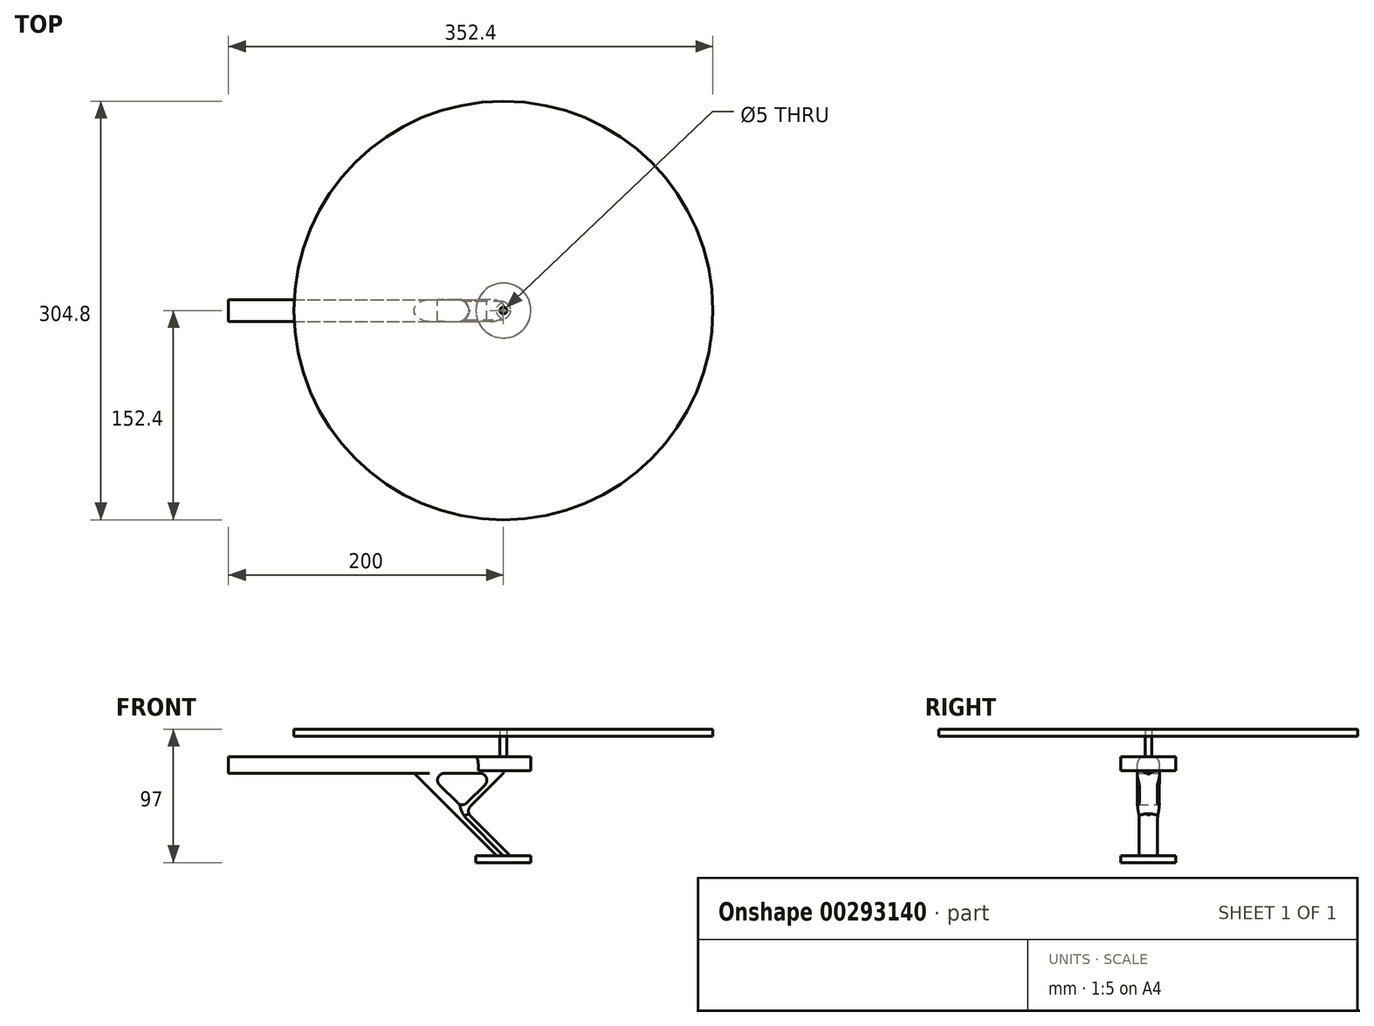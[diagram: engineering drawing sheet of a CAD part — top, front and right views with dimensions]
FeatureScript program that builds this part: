
annotation { "Feature Type Name" : "Feature", "Feature Type Description" : "" }
export const myFeature = defineFeature(function(context is Context, id is Id, definition is map)
    precondition{}
    {
        {
            var Q0;
            Q0=qCreatedBy(makeId("Front.planeOp"),FACE);
            var sketch = newSketch(context, id + "F0", { "sketchPlane" : qUnion([Q0])});
            skLineSegment(sketch, "E0.bottom", {"start": v(0, 0) * mm, "end": v(200, 0) * mm});
            skLineSegment(sketch, "E0.top", {"start": v(0, 12) * mm, "end": v(200, 12) * mm});
            skLineSegment(sketch, "E0.left", {"start": v(0, 0) * mm, "end": v(0, 12) * mm});
            skLineSegment(sketch, "E0.right", {"start": v(200, 0) * mm, "end": v(200, 12) * mm});
            skSolve(sketch);
        }
        {
            var Q0;
            Q0=makeQuery(id+"F0.imprint","IMPRINT",FACE,{"disambiguationData":[TD([[makeQuery(id+"F0.imprint","IMPRINT",EDGE,{"derivedFrom":sQuery(id+"F0.wireOp",EDGE,"E0.bottom")}),1.0]])]});
            extrude(context, id + "F1", {"entities" : qUnion([Q0]), "oppositeDirection" : true, "depth" : 16 * mm});
        }
        {
            var Q0;
            Q0=makeQuery(id+"F1.opExtrude","SWEPT_FACE",FACE,{"disambiguationData":[OSD([sQuery(id+"F0.wireOp",EDGE,"E0.top")])]});
            var sketch = newSketch(context, id + "F2", { "sketchPlane" : qUnion([Q0])});
            skCircle(sketch, "E1", {"center": v(200, 8) * mm, "radius": 20 * mm});
            skSolve(sketch);
        }
        {
            var Q0;
            {var subQ1=sQuery(id+"F0.wireOp",EDGE,"E0.top");var subQ6=makeQuery(id+"F1.opExtrude","SWEPT_EDGE",EDGE,{"disambiguationData":[OSD([subQ1,sQuery(id+"F0.wireOp",EDGE,"E0.right")])]});Q0=makeQuery(id+"F2.imprint","IMPRINT",FACE,{"disambiguationData":[TD([[makeQuery(id+"F2.imprint","IMPRINT",EDGE,{"derivedFrom":subQ6}),1.0]])]});}
            var Q1;
            {var subQ1=sQuery(id+"F0.wireOp",EDGE,"E0.top");var subQ6=makeQuery(id+"F1.opExtrude","SWEPT_EDGE",EDGE,{"disambiguationData":[OSD([subQ1,sQuery(id+"F0.wireOp",EDGE,"E0.right")])]});Q1=makeQuery(id+"F2.imprint","IMPRINT",FACE,{"disambiguationData":[TD([[makeQuery(id+"F2.imprint","IMPRINT",EDGE,{"derivedFrom":subQ6}),-1.0]])]});}
            extrude(context, id + "F3", {"entities" : qUnion([Q0, Q1]), "operationType" : NewBodyOperationType.ADD, "oppositeDirection" : true, "depth" : 10 * mm});
        }
        {
            var Q0;
            Q0=makeQuery(id+"F1.opExtrude","CAP_FACE",FACE,{"disambiguationData":[OSD([sQuery(id+"F0.wireOp",EDGE,"E0.bottom"),sQuery(id+"F0.wireOp",EDGE,"E0.top"),sQuery(id+"F0.wireOp",EDGE,"E0.left"),sQuery(id+"F0.wireOp",EDGE,"E0.right")])],"isStart":true});
            var sketch = newSketch(context, id + "F4", { "sketchPlane" : qUnion([Q0])});
            skLineSegment(sketch, "E2", {"start": v(135, 0) * mm, "end": v(195, -60) * mm});
            skLineSegment(sketch, "E3", {"start": v(205, -60) * mm, "end": v(145, 0) * mm});
            skLineSegment(sketch, "E4", {"start": v(195, -60) * mm, "end": v(205, -60) * mm});
            skLineSegment(sketch, "E5", {"start": v(135, 0) * mm, "end": v(145, 0) * mm});
            skLineSegment(sketch, "E6", {"start": v(200, 0) * mm, "end": v(172.5, -27.5) * mm});
            skLineSegment(sketch, "E7", {"start": v(200, 0) * mm, "end": v(195, 0) * mm});
            skLineSegment(sketch, "E8", {"start": v(195, 0) * mm, "end": v(170, -25) * mm});
            skSolve(sketch);
        }
        {
            var Q0;
            Q0=makeQuery(id+"F4.imprint","IMPRINT",FACE,{"disambiguationData":[TD([[makeQuery(id+"F4.imprint","IMPRINT",EDGE,{"derivedFrom":sQuery(id+"F4.wireOp",EDGE,"E2")}),1.0]])]});
            var Q1;
            {var subQ0=sQuery(id+"F4.wireOp",EDGE,"E6");Q1=makeQuery(id+"F4.imprint","IMPRINT",FACE,{"disambiguationData":[TD([[makeQuery(id+"F4.imprint","IMPRINT",EDGE,{"derivedFrom":subQ0}),-1.0]])]});}
            extrude(context, id + "F5", {"entities" : qUnion([Q0, Q1]), "operationType" : NewBodyOperationType.ADD, "oppositeDirection" : true, "depth" : 16 * mm});
        }
        {
            var Q0;
            Q0=makeQuery(id+"F5.opExtrude","SWEPT_EDGE",EDGE,{"disambiguationData":[OSD([sQuery(id+"F4.wireOp",EDGE,"E3"),sQuery(id+"F4.wireOp",EDGE,"E8")])]});
            var Q1;
            Q1=makeQuery(id+"F5.opExtrude","SWEPT_EDGE",EDGE,{"disambiguationData":[OSD([sQuery(id+"F0.wireOp",EDGE,"E0.bottom"),sQuery(id+"F4.wireOp",EDGE,"E3"),sQuery(id+"F4.wireOp",EDGE,"E5")])]});
            var Q2;
            Q2=makeQuery(id+"F5.opExtrude","SWEPT_EDGE",EDGE,{"disambiguationData":[OSD([sQuery(id+"F0.wireOp",EDGE,"E0.bottom"),sQuery(id+"F4.wireOp",EDGE,"E7"),sQuery(id+"F4.wireOp",EDGE,"E8")])]});
            var Q3;
            Q3=makeQuery(id+"F5.opExtrude","SWEPT_EDGE",EDGE,{"disambiguationData":[OSD([sQuery(id+"F4.wireOp",EDGE,"E3"),sQuery(id+"F4.wireOp",EDGE,"E6")])]});
            var Q4;
            Q4=makeQuery(id+"F5.opExtrude","SWEPT_EDGE",EDGE,{"disambiguationData":[OSD([sQuery(id+"F0.wireOp",EDGE,"E0.bottom"),sQuery(id+"F4.wireOp",EDGE,"E2"),sQuery(id+"F4.wireOp",EDGE,"E5")])]});
            fillet(context, id + "F6", {"entities" : qUnion([Q0, Q1, Q2, Q3, Q4]), "radius" : 5 * mm, "tangentPropagation" : true, "allowEdgeOverflow" : false});
        }
        {
            var Q0;
            Q0=makeQuery(id+"F5.opExtrude","SWEPT_FACE",FACE,{"disambiguationData":[OSD([sQuery(id+"F4.wireOp",EDGE,"E4")])]});
            var sketch = newSketch(context, id + "F7", { "sketchPlane" : qUnion([Q0])});
            skCircle(sketch, "E9", {"center": v(200, -8) * mm, "radius": 20 * mm});
            skSolve(sketch);
        }
        {
            var Q0;
            Q0=makeQuery(id+"F7.imprint","IMPRINT",FACE,{"disambiguationData":[TD([[makeQuery(id+"F7.imprint","IMPRINT",EDGE,{"derivedFrom":sQuery(id+"F7.wireOp",EDGE,"E9")}),1.0]])]});
            var Q1;
            {var subQ0=sQuery(id+"F4.wireOp",EDGE,"E4");Q1=makeQuery(id+"F7.imprint","IMPRINT",FACE,{"disambiguationData":[TD([[makeQuery(id+"F7.imprint","IMPRINT",EDGE,{"derivedFrom":makeQuery(id+"F5.opExtrude","CAP_EDGE",EDGE,{"disambiguationData":[OSD([subQ0])],"isStart":true})}),-1.0]])]});}
            extrude(context, id + "F8", {"entities" : qUnion([Q0, Q1]), "operationType" : NewBodyOperationType.ADD, "depth" : 5 * mm});
        }
        {
            var Q0;
            {var subQ0=sQuery(id+"F0.wireOp",EDGE,"E0.right");Q0=makeQuery(id+"F5.boolean.opBoolean","MERGE",EDGE,{"derivedFrom":[makeQuery(id+"F1.opExtrude","SWEPT_EDGE",EDGE,{"disambiguationData":[OSD([sQuery(id+"F0.wireOp",EDGE,"E0.bottom"),subQ0])]}),makeQuery(id+"F5.opExtrude","SWEPT_EDGE",EDGE,{"disambiguationData":[OSD([subQ0,sQuery(id+"F4.wireOp",EDGE,"E6"),sQuery(id+"F4.wireOp",EDGE,"E7")])]})]});}
            fillet(context, id + "F9", {"entities" : qUnion([Q0]), "radius" : 2 * mm, "tangentPropagation" : true, "allowEdgeOverflow" : false});
        }
        {
            var Q0;
            Q0=makeQuery(id+"F3.boolean.opBoolean","MERGE",FACE,{"derivedFrom":[makeQuery(id+"F1.opExtrude","SWEPT_FACE",FACE,{"disambiguationData":[OSD([sQuery(id+"F0.wireOp",EDGE,"E0.top")])]}),makeQuery(id+"F3.opExtrude","CAP_FACE",FACE,{"disambiguationData":[OSD([sQuery(id+"F2.wireOp",EDGE,"E1")])],"isStart":true})]});
            var sketch = newSketch(context, id + "F10", { "sketchPlane" : qUnion([Q0])});
            skCircle(sketch, "E10", {"center": v(200, 8) * mm, "radius": 2.5 * mm});
            skSolve(sketch);
        }
        {
            var Q0;
            Q0=makeQuery(id+"F10.imprint","IMPRINT",FACE,{"disambiguationData":[TD([[makeQuery(id+"F10.imprint","IMPRINT",EDGE,{"derivedFrom":sQuery(id+"F10.wireOp",EDGE,"E10")}),1.0]])]});
            extrude(context, id + "F11", {"entities" : qUnion([Q0]), "operationType" : NewBodyOperationType.ADD, "depth" : 15 * mm});
        }
        {
            var Q0;
            Q0=makeQuery(id+"F11.opExtrude","CAP_FACE",FACE,{"disambiguationData":[OSD([sQuery(id+"F10.wireOp",EDGE,"E10")])],"isStart":false});
            var sketch = newSketch(context, id + "F12", { "sketchPlane" : qUnion([Q0])});
            skCircle(sketch, "E11", {"center": v(200, 8) * mm, "radius": 152.4 * mm});
            skSolve(sketch);
        }
        {
            var Q0;
            Q0=makeQuery(id+"F1.opExtrude","CAP_EDGE",EDGE,{"disambiguationData":[OSD([sQuery(id+"F0.wireOp",EDGE,"E0.top")])],"isStart":false});
            var Q1;
            Q1=makeQuery(id+"F1.opExtrude","CAP_EDGE",EDGE,{"disambiguationData":[OSD([sQuery(id+"F0.wireOp",EDGE,"E0.top")])],"isStart":true});
            fillet(context, id + "F13", {"entities" : qUnion([Q0, Q1]), "radius" : 5 * mm, "tangentPropagation" : true, "allowEdgeOverflow" : false});
        }
        {
            var Q0;
            Q0=makeQuery(id+"F5.opExtrude","CAP_EDGE",EDGE,{"disambiguationData":[OSD([sQuery(id+"F4.wireOp",EDGE,"E6")])],"isStart":false});
            var Q1;
            Q1=makeQuery(id+"F5.opExtrude","CAP_EDGE",EDGE,{"disambiguationData":[OSD([sQuery(id+"F4.wireOp",EDGE,"E6")])],"isStart":true});
            fillet(context, id + "F14", {"entities" : qUnion([Q0, Q1]), "radius" : 8 * mm, "tangentPropagation" : true, "allowEdgeOverflow" : false});
        }
        {
            var Q0;
            Q0=makeQuery(id+"F5.opExtrude","CAP_EDGE",EDGE,{"disambiguationData":[OSD([sQuery(id+"F4.wireOp",EDGE,"E2")])],"isStart":false});
            var Q1;
            {var subQ0=sQuery(id+"F4.wireOp",EDGE,"E2");var subQ1=sQuery(id+"F4.wireOp",EDGE,"E6");var subQ2=sQuery(id+"F4.wireOp",EDGE,"E3");Q1=makeQuery(id+"F14.opFillet","BLEND_EDGE",EDGE,{"blendedFrom":[makeQuery(id+"F6.opFillet","BLEND_EDGE",EDGE,{"blendedFrom":[makeQuery(id+"F5.opExtrude","SWEPT_EDGE",EDGE,{"disambiguationData":[OSD([subQ2,subQ1])]}),makeQuery(id+"F5.boolean.opBoolean","MERGE",FACE,{"derivedFrom":[makeQuery(id+"F1.opExtrude","CAP_FACE",FACE,{"disambiguationData":[OSD([sQuery(id+"F0.wireOp",EDGE,"E0.bottom"),sQuery(id+"F0.wireOp",EDGE,"E0.top"),sQuery(id+"F0.wireOp",EDGE,"E0.left"),sQuery(id+"F0.wireOp",EDGE,"E0.right")])],"isStart":false}),makeQuery(id+"F5.opExtrude","CAP_FACE",FACE,{"disambiguationData":[OSD([subQ0,subQ2,sQuery(id+"F4.wireOp",EDGE,"E4"),sQuery(id+"F4.wireOp",EDGE,"E5"),subQ1,sQuery(id+"F4.wireOp",EDGE,"E7"),sQuery(id+"F4.wireOp",EDGE,"E8")])],"isStart":false})]})],"blendedInto":[makeQuery(id+"F5.boolean.opBoolean","MERGE",FACE,{"derivedFrom":[makeQuery(id+"F1.opExtrude","CAP_FACE",FACE,{"disambiguationData":[OSD([sQuery(id+"F0.wireOp",EDGE,"E0.bottom"),sQuery(id+"F0.wireOp",EDGE,"E0.top"),sQuery(id+"F0.wireOp",EDGE,"E0.left"),sQuery(id+"F0.wireOp",EDGE,"E0.right")])],"isStart":false}),makeQuery(id+"F5.opExtrude","CAP_FACE",FACE,{"disambiguationData":[OSD([subQ0,subQ2,sQuery(id+"F4.wireOp",EDGE,"E4"),sQuery(id+"F4.wireOp",EDGE,"E5"),subQ1,sQuery(id+"F4.wireOp",EDGE,"E7"),sQuery(id+"F4.wireOp",EDGE,"E8")])],"isStart":false})]})]}),makeQuery(id+"F5.opExtrude","SWEPT_FACE",FACE,{"disambiguationData":[OSD([subQ0])]})],"blendedInto":[makeQuery(id+"F5.opExtrude","SWEPT_FACE",FACE,{"disambiguationData":[OSD([subQ0])]})]});}
            var Q2;
            {var subQ0=sQuery(id+"F4.wireOp",EDGE,"E3");Q2=makeQuery(id+"F14.opFillet","BLEND_EDGE",EDGE,{"blendedFrom":[makeQuery(id+"F5.opExtrude","CAP_EDGE",EDGE,{"disambiguationData":[OSD([subQ0]),TDD([makeQuery(id+"F4.imprint","IMPRINT",EDGE,{"disambiguationData":[TD([[makeQuery(id+"F4.imprint","INTERSECT",VERTEX,{"derivedFrom":[subQ0,sQuery(id+"F4.wireOp",EDGE,"E4")]}),-1.0]])],"derivedFrom":subQ0})])],"isStart":false}),makeQuery(id+"F5.opExtrude","SWEPT_FACE",FACE,{"disambiguationData":[OSD([sQuery(id+"F4.wireOp",EDGE,"E2")])]})],"blendedInto":[makeQuery(id+"F5.opExtrude","SWEPT_FACE",FACE,{"disambiguationData":[OSD([sQuery(id+"F4.wireOp",EDGE,"E2")])]})]});}
            var Q3;
            Q3=makeQuery(id+"F5.opExtrude","CAP_EDGE",EDGE,{"disambiguationData":[OSD([sQuery(id+"F4.wireOp",EDGE,"E2")])],"isStart":true});
            var Q4;
            {var subQ0=sQuery(id+"F4.wireOp",EDGE,"E2");var subQ1=sQuery(id+"F4.wireOp",EDGE,"E6");var subQ2=sQuery(id+"F4.wireOp",EDGE,"E3");Q4=makeQuery(id+"F14.opFillet","BLEND_EDGE",EDGE,{"blendedFrom":[makeQuery(id+"F6.opFillet","BLEND_EDGE",EDGE,{"blendedFrom":[makeQuery(id+"F5.opExtrude","SWEPT_EDGE",EDGE,{"disambiguationData":[OSD([subQ2,subQ1])]}),makeQuery(id+"F5.boolean.opBoolean","MERGE",FACE,{"derivedFrom":[makeQuery(id+"F1.opExtrude","CAP_FACE",FACE,{"disambiguationData":[OSD([sQuery(id+"F0.wireOp",EDGE,"E0.bottom"),sQuery(id+"F0.wireOp",EDGE,"E0.top"),sQuery(id+"F0.wireOp",EDGE,"E0.left"),sQuery(id+"F0.wireOp",EDGE,"E0.right")])],"isStart":true}),makeQuery(id+"F5.opExtrude","CAP_FACE",FACE,{"disambiguationData":[OSD([subQ0,subQ2,sQuery(id+"F4.wireOp",EDGE,"E4"),sQuery(id+"F4.wireOp",EDGE,"E5"),subQ1,sQuery(id+"F4.wireOp",EDGE,"E7"),sQuery(id+"F4.wireOp",EDGE,"E8")])],"isStart":true})]})],"blendedInto":[makeQuery(id+"F5.boolean.opBoolean","MERGE",FACE,{"derivedFrom":[makeQuery(id+"F1.opExtrude","CAP_FACE",FACE,{"disambiguationData":[OSD([sQuery(id+"F0.wireOp",EDGE,"E0.bottom"),sQuery(id+"F0.wireOp",EDGE,"E0.top"),sQuery(id+"F0.wireOp",EDGE,"E0.left"),sQuery(id+"F0.wireOp",EDGE,"E0.right")])],"isStart":true}),makeQuery(id+"F5.opExtrude","CAP_FACE",FACE,{"disambiguationData":[OSD([subQ0,subQ2,sQuery(id+"F4.wireOp",EDGE,"E4"),sQuery(id+"F4.wireOp",EDGE,"E5"),subQ1,sQuery(id+"F4.wireOp",EDGE,"E7"),sQuery(id+"F4.wireOp",EDGE,"E8")])],"isStart":true})]})]}),makeQuery(id+"F5.opExtrude","SWEPT_FACE",FACE,{"disambiguationData":[OSD([subQ0])]})],"blendedInto":[makeQuery(id+"F5.opExtrude","SWEPT_FACE",FACE,{"disambiguationData":[OSD([subQ0])]})]});}
            var Q5;
            {var subQ0=sQuery(id+"F4.wireOp",EDGE,"E3");Q5=makeQuery(id+"F14.opFillet","BLEND_EDGE",EDGE,{"blendedFrom":[makeQuery(id+"F5.opExtrude","CAP_EDGE",EDGE,{"disambiguationData":[OSD([subQ0]),TDD([makeQuery(id+"F4.imprint","IMPRINT",EDGE,{"disambiguationData":[TD([[makeQuery(id+"F4.imprint","INTERSECT",VERTEX,{"derivedFrom":[subQ0,sQuery(id+"F4.wireOp",EDGE,"E4")]}),-1.0]])],"derivedFrom":subQ0})])],"isStart":true}),makeQuery(id+"F5.opExtrude","SWEPT_FACE",FACE,{"disambiguationData":[OSD([sQuery(id+"F4.wireOp",EDGE,"E2")])]})],"blendedInto":[makeQuery(id+"F5.opExtrude","SWEPT_FACE",FACE,{"disambiguationData":[OSD([sQuery(id+"F4.wireOp",EDGE,"E2")])]})]});}
            fillet(context, id + "F15", {"entities" : qUnion([Q0, Q1, Q2, Q3, Q4, Q5]), "radius" : 8 * mm, "tangentPropagation" : true, "allowEdgeOverflow" : false});
        }
        {
            var Q0;
            Q0=makeQuery(id+"F12.imprint","IMPRINT",FACE,{"disambiguationData":[TD([[makeQuery(id+"F12.imprint","IMPRINT",EDGE,{"derivedFrom":sQuery(id+"F12.wireOp",EDGE,"E11")}),1.0]])]});
            extrude(context, id + "F16", {"entities" : qUnion([Q0]), "depth" : 5 * mm});
        }
    });
